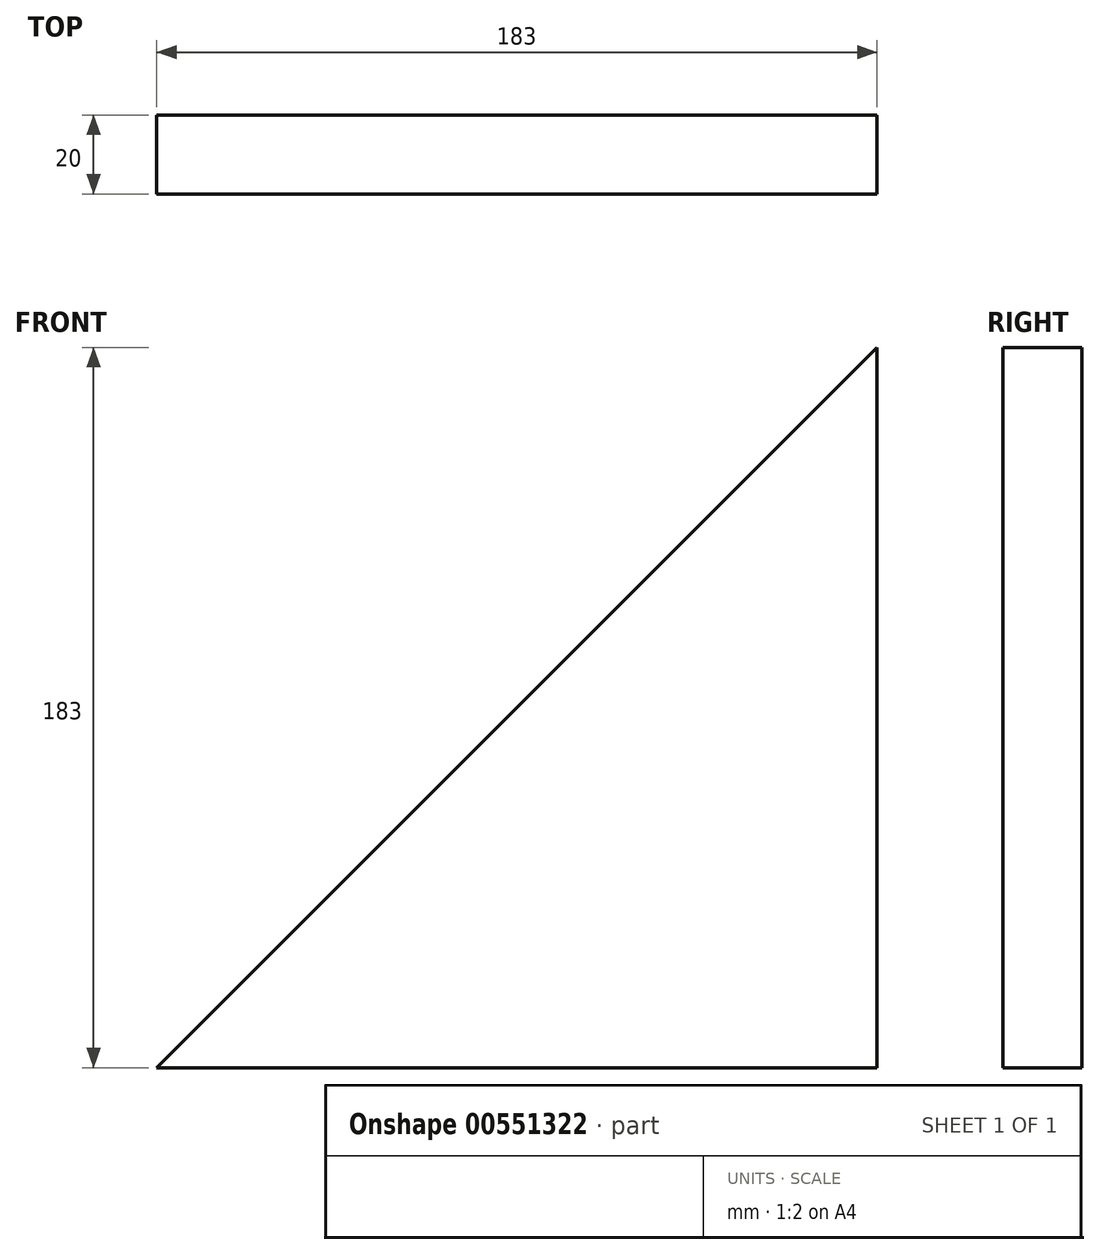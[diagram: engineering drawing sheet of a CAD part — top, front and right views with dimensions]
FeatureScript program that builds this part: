
annotation { "Feature Type Name" : "Feature", "Feature Type Description" : "" }
export const myFeature = defineFeature(function(context is Context, id is Id, definition is map)
    precondition{}
    {
        {
            var Q0;
            Q0=qCreatedBy(makeId("Front.planeOp"),FACE);
            var sketch = newSketch(context, id + "F0", { "sketchPlane" : qUnion([Q0])});
            skLineSegment(sketch, "E0.bottom", {"start": v(0, 0) * mm, "end": v(-183, 0) * mm});
            skLineSegment(sketch, "E0.left", {"start": v(0, 0) * mm, "end": v(0, 183) * mm});
            skLineSegment(sketch, "E1", {"start": v(0, 183) * mm, "end": v(-183, 0) * mm});
            skSolve(sketch);
        }
        {
            var Q0;
            Q0=makeQuery(id+"F0.imprint","IMPRINT",FACE,{"disambiguationData":[TD([[makeQuery(id+"F0.imprint","IMPRINT",EDGE,{"derivedFrom":sQuery(id+"F0.wireOp",EDGE,"E0.bottom")}),-1.0]])]});
            extrude(context, id + "F1", {"entities" : qUnion([Q0]), "depth" : 20 * mm, "offsetDistance" : 25 * mm});
        }
    });
